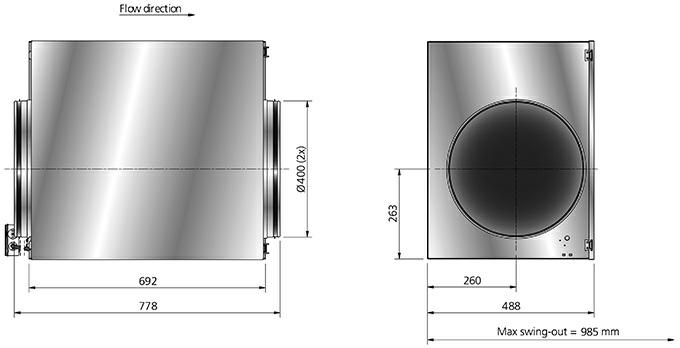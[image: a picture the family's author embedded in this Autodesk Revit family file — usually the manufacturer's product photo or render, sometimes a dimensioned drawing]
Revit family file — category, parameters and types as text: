
# Revit family: IRE 630 B3 ErP AC_
name_source: partatom
category: Mechanical Equipment
revit_build: Autodesk Revit MEP 2014 (Build: 20130308_1515(x64)
units: mm (PartAtom-declared; Revit-internal decimal feet)

## types (1)
- IRE 630 B3 ErP AC
    Capacitor = - μF
    Current = 5 A
    Depth = 955 mm  [stored 3.1332 ft]
    Description = Insulated duct fans with circular connections
    Diameter = 630 mm  [stored 2.06693 ft]
    Frequency = 50 Hz
    Height = 703 mm  [stored 2.30643 ft]
    Main Material = Steel, Galvanized
    Max. temperature of transported air = 40 °C
    Max. temperature of transported air when speed controlled = 40 °C
    Phase = 3
    Power = 2183 W
    Sound pressure level at 3 m = 48 dB(A)
    Speed = 680 rpm
    Voltage = 400 V
    Voltage range = 380-415 V
    Weight = 115.00 kg
    Width = 1067 mm  [stored 3.50066 ft]
    Wiring diagram = Y 4040004 / Δ 4040003

note: [stored X ft] marks values corroborated as IEEE doubles in the binary element streams (Revit-internal decimal feet)

## geometry (parser evidence)
native form markers: Sweep x5
no freeform markers — native parametric forms only
